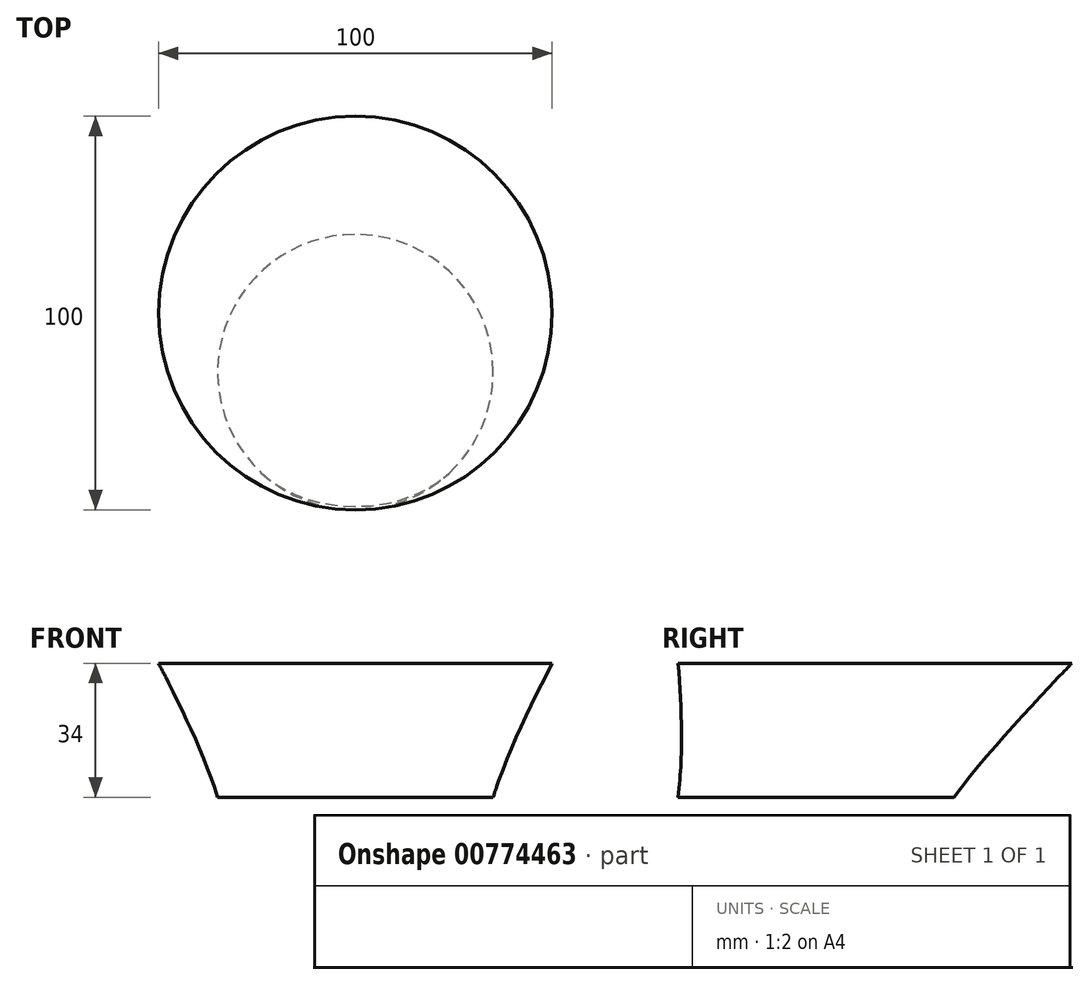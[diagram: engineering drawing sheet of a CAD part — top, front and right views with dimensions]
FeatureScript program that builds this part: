
annotation { "Feature Type Name" : "Feature", "Feature Type Description" : "" }
export const myFeature = defineFeature(function(context is Context, id is Id, definition is map)
    precondition{}
    {
        {
            var Q0;
            Q0=qCreatedBy(makeId("Top.planeOp"),FACE);
            var sketch = newSketch(context, id + "F0", { "sketchPlane" : qUnion([Q0])});
            skCircle(sketch, "E0", {"center": v(0, 0) * mm, "radius": 35 * mm});
            skSolve(sketch);
        }
        {
            var Q0;
            Q0=qCreatedBy(makeId("Top.planeOp"),FACE);
            cPlane(context, id + "F1", {"entities" : qUnion([Q0]), "cplaneType" : CPlaneType.OFFSET, "offset" : 34 * mm, "width" : 150 * mm, "height" : 150 * mm});
        }
        {
            var Q0;
            Q0=qCreatedBy(id+"F1.planeOp",FACE);
            var sketch = newSketch(context, id + "F2", { "sketchPlane" : qUnion([Q0])});
            skCircle(sketch, "E1", {"center": v(0, 15) * mm, "radius": 50 * mm});
            skLineSegment(sketch, "E2", {"start": v(0, 15) * mm, "end": v(0, 0) * mm, "construction": true});
            skSolve(sketch);
        }
        {
            var Q0;
            Q0=qCreatedBy(makeId("Right.planeOp"),FACE);
            var sketch = newSketch(context, id + "F3", { "sketchPlane" : qUnion([Q0])});
            skLineSegment(sketch, "E3", {"start": v(-35, 0) * mm, "end": v(-35, 34) * mm});
            skSolve(sketch);
        }
        {
            var Q0;
            Q0=makeQuery(id+"F0.imprint","IMPRINT",FACE,{"disambiguationData":[TD([[makeQuery(id+"F0.imprint","IMPRINT",EDGE,{"derivedFrom":sQuery(id+"F0.wireOp",EDGE,"E0")}),1.0]])]});
            var Q1;
            Q1=makeQuery(id+"F2.imprint","IMPRINT",FACE,{"disambiguationData":[TD([[makeQuery(id+"F2.imprint","IMPRINT",EDGE,{"derivedFrom":sQuery(id+"F2.wireOp",EDGE,"E1")}),1.0]])]});
            var Q2;
            Q2=sQuery(id+"F3.wireOp",EDGE,"E3");
            loft(context, id + "F4", {"sheetProfilesArray" : [{ "sheetProfileEntities" : qUnion([Q0]) }, { "sheetProfileEntities" : qUnion([Q1]) }], "addSections" : true, "spine" : qUnion([Q2]), "sectionCount" : 5});
        }
    });
